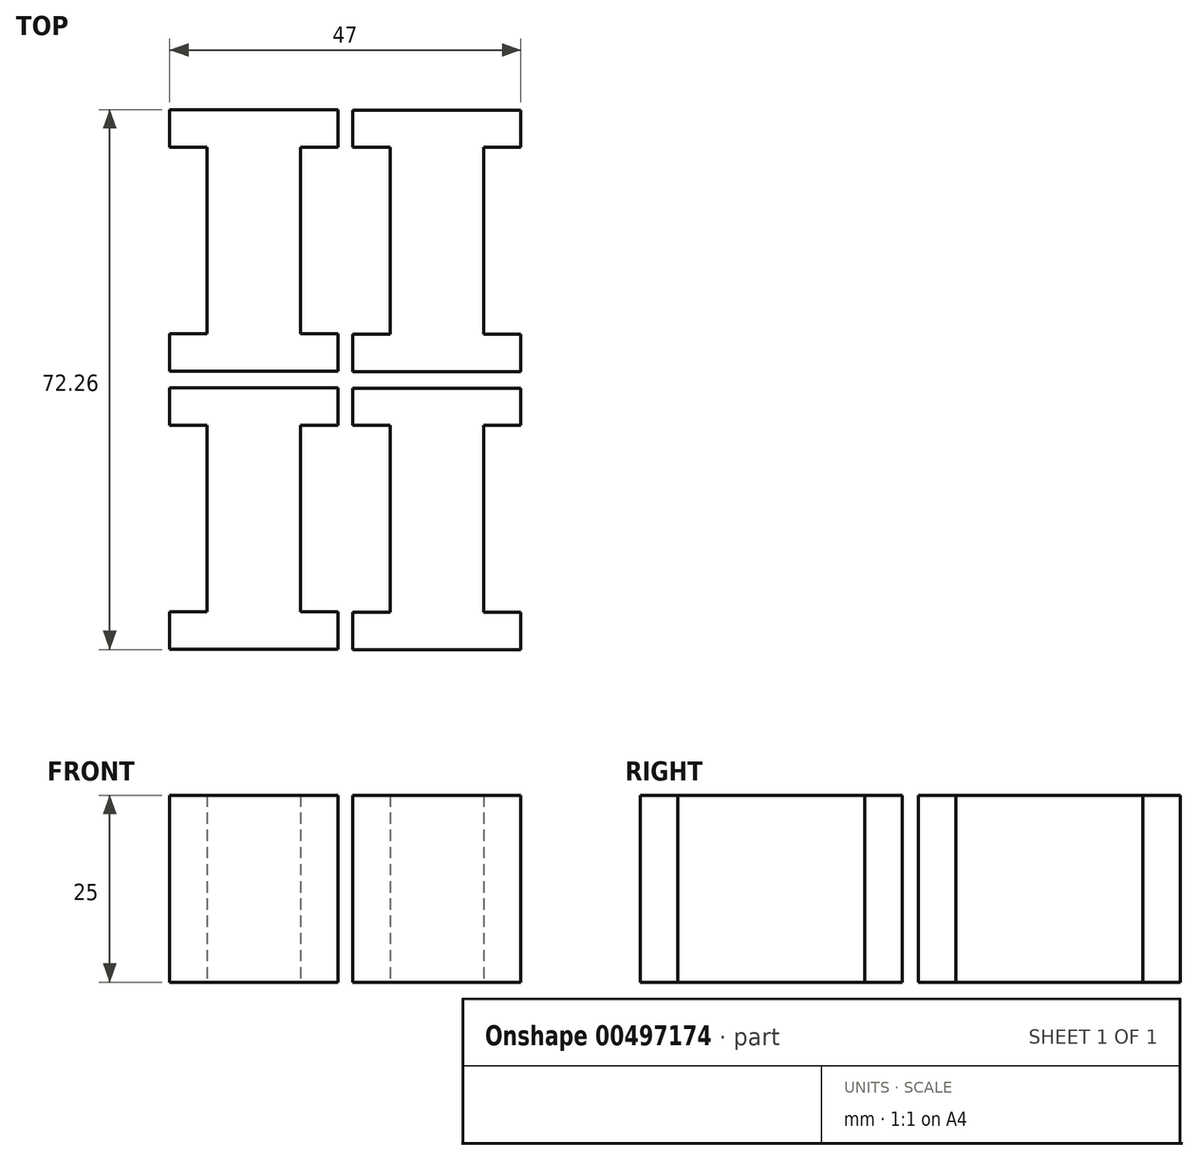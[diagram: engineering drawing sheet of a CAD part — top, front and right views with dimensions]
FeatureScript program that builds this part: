
annotation { "Feature Type Name" : "Feature", "Feature Type Description" : "" }
export const myFeature = defineFeature(function(context is Context, id is Id, definition is map)
    precondition{}
    {
        {
            var Q0;
            Q0=qCreatedBy(makeId("Top.planeOp"),FACE);
            var sketch = newSketch(context, id + "F0", { "sketchPlane" : qUnion([Q0])});
            skLineSegment(sketch, "E0", {"start": v(0, 0) * mm, "end": v(22.5, 0) * mm});
            skLineSegment(sketch, "E1", {"start": v(22.5, 0) * mm, "end": v(22.5, 5) * mm});
            skLineSegment(sketch, "E2", {"start": v(22.5, 5) * mm, "end": v(17.5, 5) * mm});
            skLineSegment(sketch, "E3", {"start": v(17.5, 5) * mm, "end": v(17.5, 30) * mm});
            skLineSegment(sketch, "E4", {"start": v(17.5, 30) * mm, "end": v(22.5, 30) * mm});
            skLineSegment(sketch, "E5", {"start": v(22.5, 30) * mm, "end": v(22.5, 35) * mm});
            skLineSegment(sketch, "E6", {"start": v(22.5, 35) * mm, "end": v(0, 35) * mm});
            skLineSegment(sketch, "E7", {"start": v(0, 35) * mm, "end": v(0, 30) * mm});
            skLineSegment(sketch, "E8", {"start": v(0, 30) * mm, "end": v(5, 30) * mm});
            skLineSegment(sketch, "E9", {"start": v(5, 30) * mm, "end": v(5, 5) * mm});
            skLineSegment(sketch, "E10", {"start": v(5, 5) * mm, "end": v(0, 5) * mm});
            skLineSegment(sketch, "E11", {"start": v(0, 5) * mm, "end": v(0, 0) * mm});
            skLineSegment(sketch, "E12", {"start": v(0, -37.21) * mm, "end": v(22.5, -37.21) * mm});
            skLineSegment(sketch, "E13", {"start": v(22.5, -37.21) * mm, "end": v(22.5, -32.21) * mm});
            skLineSegment(sketch, "E14", {"start": v(22.5, -32.21) * mm, "end": v(17.5, -32.21) * mm});
            skLineSegment(sketch, "E15", {"start": v(17.5, -32.21) * mm, "end": v(17.5, -7.21) * mm});
            skLineSegment(sketch, "E16", {"start": v(17.5, -7.21) * mm, "end": v(22.5, -7.21) * mm});
            skLineSegment(sketch, "E17", {"start": v(22.5, -7.21) * mm, "end": v(22.5, -2.21) * mm});
            skLineSegment(sketch, "E18", {"start": v(22.5, -2.21) * mm, "end": v(0, -2.21) * mm});
            skLineSegment(sketch, "E19", {"start": v(0, -2.21) * mm, "end": v(0, -7.21) * mm});
            skLineSegment(sketch, "E20", {"start": v(0, -7.21) * mm, "end": v(5, -7.21) * mm});
            skLineSegment(sketch, "E21", {"start": v(5, -7.21) * mm, "end": v(5, -32.21) * mm});
            skLineSegment(sketch, "E22", {"start": v(5, -32.21) * mm, "end": v(0, -32.21) * mm});
            skLineSegment(sketch, "E23", {"start": v(0, -32.21) * mm, "end": v(0, -37.21) * mm});
            skLineSegment(sketch, "E24", {"start": v(-24.5, 0.05) * mm, "end": v(-2, 0.05) * mm});
            skLineSegment(sketch, "E25", {"start": v(-2, 0.05) * mm, "end": v(-2, 5.05) * mm});
            skLineSegment(sketch, "E26", {"start": v(-2, 5.05) * mm, "end": v(-7, 5.05) * mm});
            skLineSegment(sketch, "E27", {"start": v(-7, 5.05) * mm, "end": v(-7, 30.05) * mm});
            skLineSegment(sketch, "E28", {"start": v(-7, 30.05) * mm, "end": v(-2, 30.05) * mm});
            skLineSegment(sketch, "E29", {"start": v(-2, 30.05) * mm, "end": v(-2, 35.05) * mm});
            skLineSegment(sketch, "E30", {"start": v(-2, 35.05) * mm, "end": v(-24.5, 35.05) * mm});
            skLineSegment(sketch, "E31", {"start": v(-24.5, 35.05) * mm, "end": v(-24.5, 30.05) * mm});
            skLineSegment(sketch, "E32", {"start": v(-24.5, 30.05) * mm, "end": v(-19.5, 30.05) * mm});
            skLineSegment(sketch, "E33", {"start": v(-19.5, 30.05) * mm, "end": v(-19.5, 5.05) * mm});
            skLineSegment(sketch, "E34", {"start": v(-19.5, 5.05) * mm, "end": v(-24.5, 5.05) * mm});
            skLineSegment(sketch, "E35", {"start": v(-24.5, 5.05) * mm, "end": v(-24.5, 0.05) * mm});
            skLineSegment(sketch, "E36", {"start": v(-24.5, -37.16) * mm, "end": v(-2, -37.16) * mm});
            skLineSegment(sketch, "E37", {"start": v(-2, -37.16) * mm, "end": v(-2, -32.16) * mm});
            skLineSegment(sketch, "E38", {"start": v(-2, -32.16) * mm, "end": v(-7, -32.16) * mm});
            skLineSegment(sketch, "E39", {"start": v(-7, -32.16) * mm, "end": v(-7, -7.16) * mm});
            skLineSegment(sketch, "E40", {"start": v(-7, -7.16) * mm, "end": v(-2, -7.16) * mm});
            skLineSegment(sketch, "E41", {"start": v(-2, -7.16) * mm, "end": v(-2, -2.16) * mm});
            skLineSegment(sketch, "E42", {"start": v(-2, -2.16) * mm, "end": v(-24.5, -2.16) * mm});
            skLineSegment(sketch, "E43", {"start": v(-24.5, -2.16) * mm, "end": v(-24.5, -7.16) * mm});
            skLineSegment(sketch, "E44", {"start": v(-24.5, -7.16) * mm, "end": v(-19.5, -7.16) * mm});
            skLineSegment(sketch, "E45", {"start": v(-19.5, -7.16) * mm, "end": v(-19.5, -32.16) * mm});
            skLineSegment(sketch, "E46", {"start": v(-19.5, -32.16) * mm, "end": v(-24.5, -32.16) * mm});
            skLineSegment(sketch, "E47", {"start": v(-24.5, -32.16) * mm, "end": v(-24.5, -37.16) * mm});
            skSolve(sketch);
        }
        {
            var Q0;
            Q0=makeQuery(id+"F0.imprint","IMPRINT",FACE,{"disambiguationData":[TD([[makeQuery(id+"F0.imprint","IMPRINT",EDGE,{"derivedFrom":sQuery(id+"F0.wireOp",EDGE,"E0")}),1.0]])]});
            var Q1;
            Q1=makeQuery(id+"F0.imprint","IMPRINT",FACE,{"disambiguationData":[TD([[makeQuery(id+"F0.imprint","IMPRINT",EDGE,{"derivedFrom":sQuery(id+"F0.wireOp",EDGE,"E36")}),1.0]])]});
            var Q2;
            Q2=makeQuery(id+"F0.imprint","IMPRINT",FACE,{"disambiguationData":[TD([[makeQuery(id+"F0.imprint","IMPRINT",EDGE,{"derivedFrom":sQuery(id+"F0.wireOp",EDGE,"E12")}),1.0]])]});
            var Q3;
            Q3=makeQuery(id+"F0.imprint","IMPRINT",FACE,{"disambiguationData":[TD([[makeQuery(id+"F0.imprint","IMPRINT",EDGE,{"derivedFrom":sQuery(id+"F0.wireOp",EDGE,"E24")}),1.0]])]});
            extrude(context, id + "F1", {"entities" : qUnion([Q0, Q1, Q2, Q3]), "depth" : 25 * mm});
        }
    });
